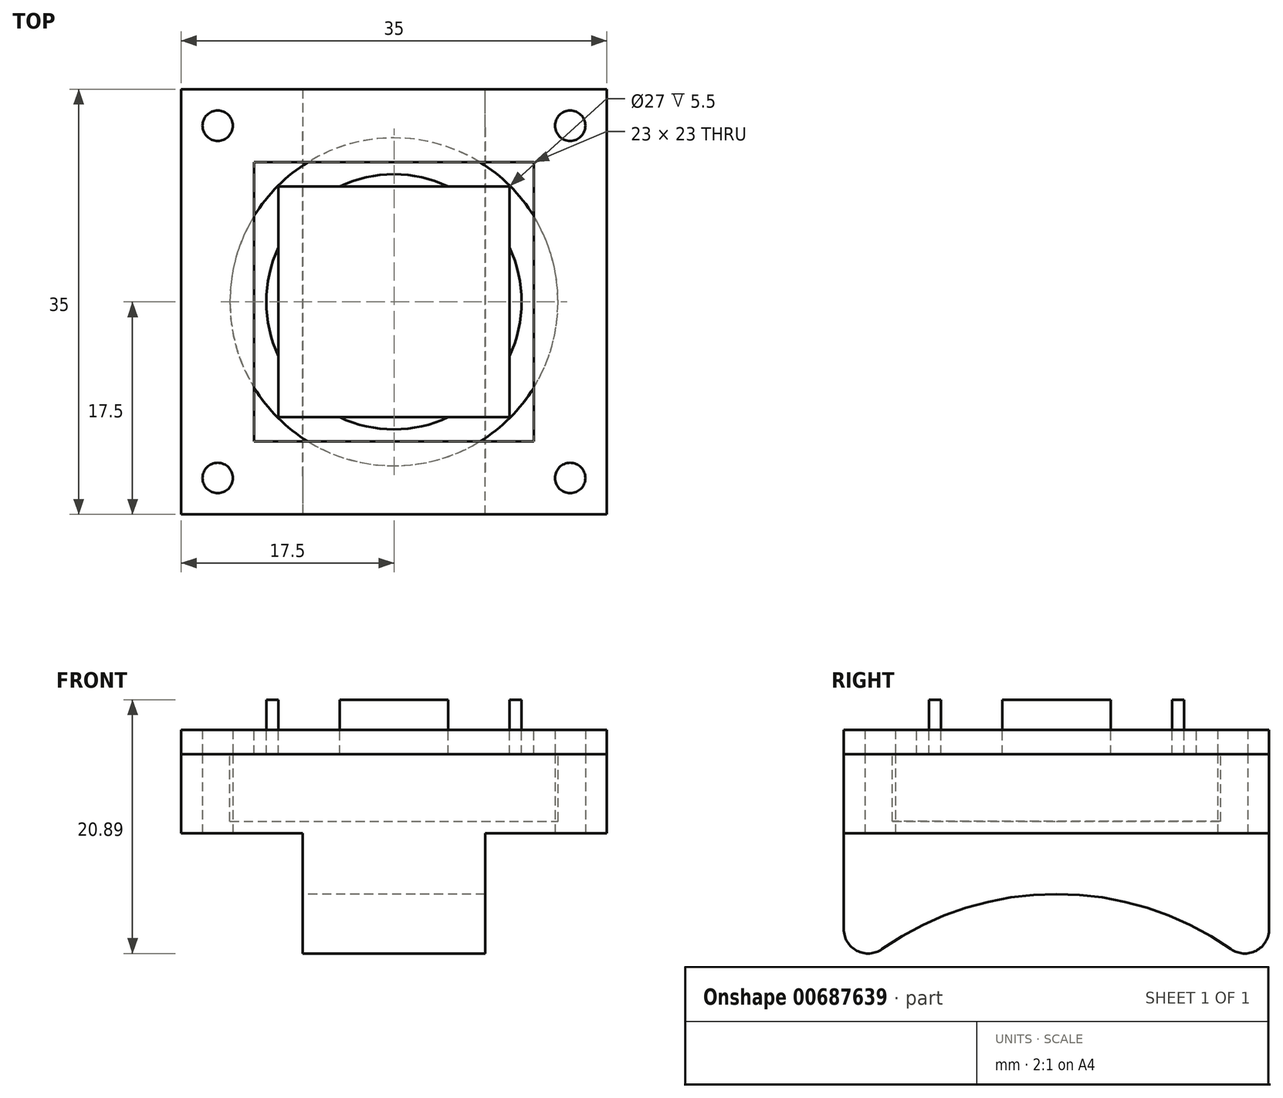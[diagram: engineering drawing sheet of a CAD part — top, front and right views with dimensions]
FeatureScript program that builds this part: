
annotation { "Feature Type Name" : "Feature", "Feature Type Description" : "" }
export const myFeature = defineFeature(function(context is Context, id is Id, definition is map)
    precondition{}
    {
        {
            var Q0;
            Q0=qCreatedBy(makeId("Top.planeOp"),FACE);
            var sketch = newSketch(context, id + "F0", { "sketchPlane" : qUnion([Q0])});
            skLineSegment(sketch, "E0", {"start": v(0, 0) * mm, "end": v(-19, 0) * mm});
            skLineSegment(sketch, "E1", {"start": v(-19, 0) * mm, "end": v(-19, 19) * mm});
            skLineSegment(sketch, "E2", {"start": v(-19, 19) * mm, "end": v(0, 19) * mm});
            skLineSegment(sketch, "E3", {"start": v(0, 19) * mm, "end": v(0, 0) * mm});
            skLineSegment(sketch, "E4.0", {"start": v(2, -2) * mm, "end": v(-21, -2) * mm});
            skLineSegment(sketch, "E4.1", {"start": v(2, 21) * mm, "end": v(2, -2) * mm});
            skLineSegment(sketch, "E4.2", {"start": v(-21, 21) * mm, "end": v(2, 21) * mm});
            skLineSegment(sketch, "E4.3", {"start": v(-21, -2) * mm, "end": v(-21, 21) * mm});
            skCircle(sketch, "E5", {"center": v(-9.5, 9.5) * mm, "radius": 10.5 * mm});
            skPoint(sketch, "E5.centerSnap0", {"position": v(-9.5, 0) * mm});
            skPoint(sketch, "E5.centerSnap1", {"position": v(0, 9.5) * mm});
            skLineSegment(sketch, "E6.0", {"start": v(8, -8) * mm, "end": v(-27, -8) * mm});
            skLineSegment(sketch, "E6.1", {"start": v(8, 27) * mm, "end": v(8, -8) * mm});
            skLineSegment(sketch, "E6.2", {"start": v(-27, 27) * mm, "end": v(8, 27) * mm});
            skLineSegment(sketch, "E6.3", {"start": v(-27, -8) * mm, "end": v(-27, 27) * mm});
            skLineSegment(sketch, "E7", {"start": v(-27, -8) * mm, "end": v(-21, -2) * mm});
            skLineSegment(sketch, "E8", {"start": v(-27, -8) * mm, "end": v(-24, -5) * mm});
            skLineSegment(sketch, "E9", {"start": v(-9.5, 9.5) * mm, "end": v(-11.5, 9.5) * mm});
            skLineSegment(sketch, "E10", {"start": v(-9.5, 9.5) * mm, "end": v(-9.5, 11.53) * mm});
            skLineSegment(sketch, "E11.MirrorCS", {"start": v(-27, 27) * mm, "end": v(-24, 24) * mm});
            skLineSegment(sketch, "E12.MirrorCS", {"start": v(8, -8) * mm, "end": v(5, -5) * mm});
            skLineSegment(sketch, "E13.MirrorCS", {"start": v(8, 27) * mm, "end": v(5, 24) * mm});
            skSolve(sketch);
        }
        {
            var Q0;
            Q0 = qSketchRegion(id + "F0", true);
            var Q1;
            {var subQ0=sQuery(id+"F0.wireOp",EDGE,"E5");var subQ1=sQuery(id+"F0.wireOp",EDGE,"E3");var subQ2=makeQuery(id+"F0.imprint","INTERSECT",VERTEX,{"disambiguationData":[OD(0.0)],"derivedFrom":[subQ1,subQ0]});Q1=makeQuery(id+"F0.imprint","IMPRINT",FACE,{"disambiguationData":[TD([[makeQuery(id+"F0.imprint","IMPRINT",EDGE,{"disambiguationData":[TD([[subQ2,-1.0]])],"derivedFrom":subQ1}),1.0]])]});}
            var Q2;
            {var subQ0=sQuery(id+"F0.wireOp",EDGE,"E5");var subQ1=sQuery(id+"F0.wireOp",EDGE,"E0");var subQ2=makeQuery(id+"F0.imprint","INTERSECT",VERTEX,{"disambiguationData":[OD(0.0)],"derivedFrom":[subQ1,subQ0]});Q2=makeQuery(id+"F0.imprint","IMPRINT",FACE,{"disambiguationData":[TD([[makeQuery(id+"F0.imprint","IMPRINT",EDGE,{"disambiguationData":[TD([[subQ2,-1.0]])],"derivedFrom":subQ1}),1.0]])]});}
            var Q3;
            {var subQ0=sQuery(id+"F0.wireOp",EDGE,"E5");var subQ1=sQuery(id+"F0.wireOp",EDGE,"E1");var subQ2=makeQuery(id+"F0.imprint","INTERSECT",VERTEX,{"disambiguationData":[OD(0.0)],"derivedFrom":[subQ1,subQ0]});Q3=makeQuery(id+"F0.imprint","IMPRINT",FACE,{"disambiguationData":[TD([[makeQuery(id+"F0.imprint","IMPRINT",EDGE,{"disambiguationData":[TD([[subQ2,-1.0]])],"derivedFrom":subQ1}),1.0]])]});}
            var Q4;
            {var subQ0=sQuery(id+"F0.wireOp",EDGE,"E5");var subQ1=sQuery(id+"F0.wireOp",EDGE,"E2");var subQ2=makeQuery(id+"F0.imprint","INTERSECT",VERTEX,{"disambiguationData":[OD(0.0)],"derivedFrom":[subQ1,subQ0]});Q4=makeQuery(id+"F0.imprint","IMPRINT",FACE,{"disambiguationData":[TD([[makeQuery(id+"F0.imprint","IMPRINT",EDGE,{"disambiguationData":[TD([[subQ2,-1.0]])],"derivedFrom":subQ1}),1.0]])]});}
            var Q5;
            {var subQ0=sQuery(id+"F0.wireOp",EDGE,"E2");var subQ1=sQuery(id+"F0.wireOp",EDGE,"E1");var subQ2=makeQuery(id+"F0.imprint","INTERSECT",VERTEX,{"derivedFrom":[subQ1,subQ0]});Q5=makeQuery(id+"F0.imprint","IMPRINT",FACE,{"disambiguationData":[TD([[makeQuery(id+"F0.imprint","IMPRINT",EDGE,{"disambiguationData":[TD([[subQ2,1.0]])],"derivedFrom":subQ1}),-1.0]])]});}
            var Q6;
            {var subQ0=sQuery(id+"F0.wireOp",EDGE,"E3");var subQ1=sQuery(id+"F0.wireOp",EDGE,"E2");var subQ2=makeQuery(id+"F0.imprint","INTERSECT",VERTEX,{"derivedFrom":[subQ1,subQ0]});Q6=makeQuery(id+"F0.imprint","IMPRINT",FACE,{"disambiguationData":[TD([[makeQuery(id+"F0.imprint","IMPRINT",EDGE,{"disambiguationData":[TD([[subQ2,1.0]])],"derivedFrom":subQ1}),-1.0]])]});}
            var Q7;
            {var subQ0=sQuery(id+"F0.wireOp",EDGE,"E3");var subQ1=sQuery(id+"F0.wireOp",EDGE,"E0");var subQ2=makeQuery(id+"F0.imprint","INTERSECT",VERTEX,{"derivedFrom":[subQ1,subQ0]});Q7=makeQuery(id+"F0.imprint","IMPRINT",FACE,{"disambiguationData":[TD([[makeQuery(id+"F0.imprint","IMPRINT",EDGE,{"disambiguationData":[TD([[subQ2,-1.0]])],"derivedFrom":subQ1}),-1.0]])]});}
            var Q8;
            {var subQ0=sQuery(id+"F0.wireOp",EDGE,"E1");var subQ1=sQuery(id+"F0.wireOp",EDGE,"E0");var subQ2=makeQuery(id+"F0.imprint","INTERSECT",VERTEX,{"derivedFrom":[subQ1,subQ0]});Q8=makeQuery(id+"F0.imprint","IMPRINT",FACE,{"disambiguationData":[TD([[makeQuery(id+"F0.imprint","IMPRINT",EDGE,{"disambiguationData":[TD([[subQ2,1.0]])],"derivedFrom":subQ1}),-1.0]])]});}
            var Q9;
            Q9=makeQuery(id+"F0.imprint","IMPRINT",FACE,{"disambiguationData":[TD([[makeQuery(id+"F0.imprint","IMPRINT",EDGE,{"derivedFrom":sQuery(id+"F0.wireOp",EDGE,"E4.0")}),-1.0]])]});
            var Q10;
            {var subQ0=sQuery(id+"F0.wireOp",EDGE,"E5");var subQ10=sQuery(id+"F0.wireOp",EDGE,"E0");var subQ11=makeQuery(id+"F0.imprint","INTERSECT",VERTEX,{"disambiguationData":[OD(0.0)],"derivedFrom":[subQ10,subQ0]});Q10=makeQuery(id+"F0.imprint","IMPRINT",FACE,{"disambiguationData":[TD([[makeQuery(id+"F0.imprint","IMPRINT",EDGE,{"disambiguationData":[TD([[subQ11,-1.0]])],"derivedFrom":subQ10}),-1.0]])]});}
            extrude(context, id + "F1", {"entities" : qUnion([Q0, Q1, Q2, Q3, Q4, Q5, Q6, Q7, Q8, Q9, Q10]), "oppositeDirection" : true, "depth" : 2 * mm, "offsetDistance" : 25 * mm});
        }
        {
            var Q0;
            Q0=makeQuery(id+"F1.opExtrude","CAP_FACE",FACE,{"disambiguationData":[OSD([sQuery(id+"F0.wireOp",EDGE,"E6.0"),sQuery(id+"F0.wireOp",EDGE,"E6.1"),sQuery(id+"F0.wireOp",EDGE,"E6.2"),sQuery(id+"F0.wireOp",EDGE,"E6.3")])],"isStart":false});
            var sketch = newSketch(context, id + "F2", { "sketchPlane" : qUnion([Q0])});
            skLineSegment(sketch, "E14", {"start": v(-27, -27) * mm, "end": v(-27, 8) * mm});
            skLineSegment(sketch, "E15", {"start": v(-27, 8) * mm, "end": v(8, 8) * mm});
            skLineSegment(sketch, "E16", {"start": v(8, 8) * mm, "end": v(8, -27) * mm});
            skLineSegment(sketch, "E17", {"start": v(8, -27) * mm, "end": v(-27, -27) * mm});
            skLineSegment(sketch, "E18", {"start": v(-27, -9.5) * mm, "end": v(8, -9.5) * mm});
            skCircle(sketch, "E19", {"center": v(-9.5, -9.5) * mm, "radius": 13.5 * mm});
            skSolve(sketch);
        }
        {
            var Q0;
            Q0 = qSketchRegion(id + "F2", true);
            extrude(context, id + "F3", {"entities" : qUnion([Q0]), "depth" : 5.5 * mm, "offsetDistance" : 25 * mm});
        }
        {
            var Q0;
            {var subQ0=sQuery(id+"F0.wireOp",EDGE,"E5");var subQ1=sQuery(id+"F0.wireOp",EDGE,"E1");var subQ2=makeQuery(id+"F0.imprint","INTERSECT",VERTEX,{"disambiguationData":[OD(0.0)],"derivedFrom":[subQ1,subQ0]});Q0=makeQuery(id+"F0.imprint","IMPRINT",FACE,{"disambiguationData":[TD([[makeQuery(id+"F0.imprint","IMPRINT",EDGE,{"disambiguationData":[TD([[subQ2,-1.0]])],"derivedFrom":subQ1}),1.0]])]});}
            var Q1;
            {var subQ0=sQuery(id+"F0.wireOp",EDGE,"E5");var subQ1=sQuery(id+"F0.wireOp",EDGE,"E2");var subQ2=makeQuery(id+"F0.imprint","INTERSECT",VERTEX,{"disambiguationData":[OD(0.0)],"derivedFrom":[subQ1,subQ0]});Q1=makeQuery(id+"F0.imprint","IMPRINT",FACE,{"disambiguationData":[TD([[makeQuery(id+"F0.imprint","IMPRINT",EDGE,{"disambiguationData":[TD([[subQ2,-1.0]])],"derivedFrom":subQ1}),1.0]])]});}
            var Q2;
            {var subQ0=sQuery(id+"F0.wireOp",EDGE,"E5");var subQ1=sQuery(id+"F0.wireOp",EDGE,"E3");var subQ2=makeQuery(id+"F0.imprint","INTERSECT",VERTEX,{"disambiguationData":[OD(0.0)],"derivedFrom":[subQ1,subQ0]});Q2=makeQuery(id+"F0.imprint","IMPRINT",FACE,{"disambiguationData":[TD([[makeQuery(id+"F0.imprint","IMPRINT",EDGE,{"disambiguationData":[TD([[subQ2,-1.0]])],"derivedFrom":subQ1}),1.0]])]});}
            var Q3;
            {var subQ0=sQuery(id+"F0.wireOp",EDGE,"E5");var subQ1=sQuery(id+"F0.wireOp",EDGE,"E0");var subQ2=makeQuery(id+"F0.imprint","INTERSECT",VERTEX,{"disambiguationData":[OD(0.0)],"derivedFrom":[subQ1,subQ0]});Q3=makeQuery(id+"F0.imprint","IMPRINT",FACE,{"disambiguationData":[TD([[makeQuery(id+"F0.imprint","IMPRINT",EDGE,{"disambiguationData":[TD([[subQ2,-1.0]])],"derivedFrom":subQ1}),1.0]])]});}
            var Q4;
            Q4=makeQuery(id+"F0.imprint","IMPRINT",FACE,{"disambiguationData":[TD([[makeQuery(id+"F0.imprint","IMPRINT",EDGE,{"derivedFrom":sQuery(id+"F0.wireOp",EDGE,"E4.0")}),-1.0]])]});
            extrude(context, id + "F4", {"entities" : qUnion([Q0, Q1, Q2, Q3, Q4]), "operationType" : NewBodyOperationType.ADD, "depth" : 2.5 * mm, "offsetDistance" : 25 * mm});
        }
        {
            var Q0;
            Q0=makeQuery(id+"F3.opExtrude","CAP_FACE",FACE,{"disambiguationData":[OSD([sQuery(id+"F2.wireOp",EDGE,"E14"),sQuery(id+"F2.wireOp",EDGE,"E15"),sQuery(id+"F2.wireOp",EDGE,"E16"),sQuery(id+"F2.wireOp",EDGE,"E17"),sQuery(id+"F2.wireOp",EDGE,"E19")])],"isStart":false});
            var Q1;
            Q1=makeQuery(id+"F1.opExtrude","CAP_FACE",FACE,{"disambiguationData":[OSD([sQuery(id+"F0.wireOp",EDGE,"E6.0"),sQuery(id+"F0.wireOp",EDGE,"E6.1"),sQuery(id+"F0.wireOp",EDGE,"E6.2"),sQuery(id+"F0.wireOp",EDGE,"E6.3")])],"isStart":false});
            extrude(context, id + "F5", {"entities" : qUnion([Q0, Q1]), "depth" : 1 * mm, "offsetDistance" : 25 * mm});
        }
        {
            var Q0;
            Q0=makeQuery(id+"F5.opExtrude","SWEPT_BODY",BODY,{"disambiguationData":[OSD([sQuery(id+"F2.wireOp",EDGE,"E14"),sQuery(id+"F2.wireOp",EDGE,"E15"),sQuery(id+"F2.wireOp",EDGE,"E16"),sQuery(id+"F2.wireOp",EDGE,"E17"),sQuery(id+"F2.wireOp",EDGE,"E19")])]});
            var Q1;
            Q1=makeQuery(id+"F5.opExtrude","SWEPT_BODY",BODY,{"disambiguationData":[OSD([sQuery(id+"F0.wireOp",EDGE,"E6.0"),sQuery(id+"F0.wireOp",EDGE,"E6.1"),sQuery(id+"F0.wireOp",EDGE,"E6.2"),sQuery(id+"F0.wireOp",EDGE,"E6.3")])]});
            deleteBodies(context, id + "F6", {"entities" : qUnion([Q0, Q1])});
        }
        {
            var Q0;
            Q0=makeQuery(id+"F3.opExtrude","CAP_FACE",FACE,{"disambiguationData":[OSD([sQuery(id+"F2.wireOp",EDGE,"E14"),sQuery(id+"F2.wireOp",EDGE,"E15"),sQuery(id+"F2.wireOp",EDGE,"E16"),sQuery(id+"F2.wireOp",EDGE,"E17"),sQuery(id+"F2.wireOp",EDGE,"E19")])],"isStart":false});
            var sketch = newSketch(context, id + "F7", { "sketchPlane" : qUnion([Q0])});
            skLineSegment(sketch, "E20", {"start": v(-27, -27) * mm, "end": v(8, -27) * mm});
            skLineSegment(sketch, "E21", {"start": v(8, -27) * mm, "end": v(8, 8) * mm});
            skLineSegment(sketch, "E22", {"start": v(8, 8) * mm, "end": v(-27, 8) * mm});
            skLineSegment(sketch, "E23", {"start": v(-27, 8) * mm, "end": v(-27, -27) * mm});
            skSolve(sketch);
        }
        {
            var Q0;
            Q0=makeQuery(id+"F7.imprint","IMPRINT",FACE,{"disambiguationData":[TD([[makeQuery(id+"F7.imprint","IMPRINT",EDGE,{"derivedFrom":sQuery(id+"F7.wireOp",EDGE,"E20")}),1.0]])]});
            var Q1;
            Q1=makeQuery(id+"F7.imprint","IMPRINT",FACE,{"disambiguationData":[TD([[makeQuery(id+"F7.imprint","IMPRINT",EDGE,{"derivedFrom":makeQuery(id+"FP3SZp29wrBzVes_1.hole-0.boolean.opBoolean","INTERSECT",EDGE,{"derivedFrom":[makeQuery(id+"F3.opExtrude","CAP_FACE",FACE,{"disambiguationData":[OSD([sQuery(id+"F2.wireOp",EDGE,"E14"),sQuery(id+"F2.wireOp",EDGE,"E15"),sQuery(id+"F2.wireOp",EDGE,"E16"),sQuery(id+"F2.wireOp",EDGE,"E17"),sQuery(id+"F2.wireOp",EDGE,"E19")])],"isStart":false}),makeQuery(id+"FP3SZp29wrBzVes_1.hole-0.opRevolve","SWEPT_FACE",FACE,{"disambiguationData":[OSD([sQuery(id+"FP3SZp29wrBzVes_1.hole-0.sketch.wireOp",EDGE,"core_line_2")])]})]})}),-1.0]])]});
            var Q2;
            Q2=makeQuery(id+"F7.imprint","IMPRINT",FACE,{"disambiguationData":[TD([[makeQuery(id+"F7.imprint","IMPRINT",EDGE,{"derivedFrom":makeQuery(id+"FP3SZp29wrBzVes_1.hole-1.boolean.opBoolean","INTERSECT",EDGE,{"derivedFrom":[makeQuery(id+"F3.opExtrude","CAP_FACE",FACE,{"disambiguationData":[OSD([sQuery(id+"F2.wireOp",EDGE,"E14"),sQuery(id+"F2.wireOp",EDGE,"E15"),sQuery(id+"F2.wireOp",EDGE,"E16"),sQuery(id+"F2.wireOp",EDGE,"E17"),sQuery(id+"F2.wireOp",EDGE,"E19")])],"isStart":false}),makeQuery(id+"FP3SZp29wrBzVes_1.hole-1.opRevolve","SWEPT_FACE",FACE,{"disambiguationData":[OSD([sQuery(id+"FP3SZp29wrBzVes_1.hole-1.sketch.wireOp",EDGE,"core_line_2")])]})]})}),-1.0]])]});
            var Q3;
            Q3=makeQuery(id+"F7.imprint","IMPRINT",FACE,{"disambiguationData":[TD([[makeQuery(id+"F7.imprint","IMPRINT",EDGE,{"derivedFrom":makeQuery(id+"FP3SZp29wrBzVes_1.hole-3.boolean.opBoolean","INTERSECT",EDGE,{"derivedFrom":[makeQuery(id+"F3.opExtrude","CAP_FACE",FACE,{"disambiguationData":[OSD([sQuery(id+"F2.wireOp",EDGE,"E14"),sQuery(id+"F2.wireOp",EDGE,"E15"),sQuery(id+"F2.wireOp",EDGE,"E16"),sQuery(id+"F2.wireOp",EDGE,"E17"),sQuery(id+"F2.wireOp",EDGE,"E19")])],"isStart":false}),makeQuery(id+"FP3SZp29wrBzVes_1.hole-3.opRevolve","SWEPT_FACE",FACE,{"disambiguationData":[OSD([sQuery(id+"FP3SZp29wrBzVes_1.hole-3.sketch.wireOp",EDGE,"core_line_2")])]})]})}),-1.0]])]});
            var Q4;
            Q4=makeQuery(id+"F7.imprint","IMPRINT",FACE,{"disambiguationData":[TD([[makeQuery(id+"F7.imprint","IMPRINT",EDGE,{"derivedFrom":makeQuery(id+"F3.opExtrude","CAP_EDGE",EDGE,{"disambiguationData":[OSD([sQuery(id+"F2.wireOp",EDGE,"E19")])],"isStart":false})}),1.0]])]});
            var Q5;
            Q5=makeQuery(id+"F7.imprint","IMPRINT",FACE,{"disambiguationData":[TD([[makeQuery(id+"F7.imprint","IMPRINT",EDGE,{"derivedFrom":makeQuery(id+"FP3SZp29wrBzVes_1.hole-2.boolean.opBoolean","INTERSECT",EDGE,{"derivedFrom":[makeQuery(id+"F3.opExtrude","CAP_FACE",FACE,{"disambiguationData":[OSD([sQuery(id+"F2.wireOp",EDGE,"E14"),sQuery(id+"F2.wireOp",EDGE,"E15"),sQuery(id+"F2.wireOp",EDGE,"E16"),sQuery(id+"F2.wireOp",EDGE,"E17"),sQuery(id+"F2.wireOp",EDGE,"E19")])],"isStart":false}),makeQuery(id+"FP3SZp29wrBzVes_1.hole-2.opRevolve","SWEPT_FACE",FACE,{"disambiguationData":[OSD([sQuery(id+"FP3SZp29wrBzVes_1.hole-2.sketch.wireOp",EDGE,"core_line_2")])]})]})}),-1.0]])]});
            extrude(context, id + "F8", {"entities" : qUnion([Q0, Q1, Q2, Q3, Q4, Q5]), "operationType" : NewBodyOperationType.ADD, "depth" : 1 * mm, "offsetDistance" : 25 * mm});
        }
        {
            var Q0;
            Q0=sQuery(id+"F0.wireOp",VERTEX,"E8.end");
            var Q1;
            Q1=sQuery(id+"F0.wireOp",VERTEX,"E11.MirrorCS.end");
            var Q2;
            Q2=sQuery(id+"F0.wireOp",VERTEX,"E13.MirrorCS.end");
            var Q3;
            Q3=sQuery(id+"F0.wireOp",VERTEX,"E12.MirrorCS.end");
            var Q4;
            Q4=makeQuery(id+"F3.opExtrude","SWEPT_BODY",BODY,{"disambiguationData":[OSD([sQuery(id+"F2.wireOp",EDGE,"E14"),sQuery(id+"F2.wireOp",EDGE,"E15"),sQuery(id+"F2.wireOp",EDGE,"E16"),sQuery(id+"F2.wireOp",EDGE,"E17"),sQuery(id+"F2.wireOp",EDGE,"E19")])]});
            var Q5;
            Q5=makeQuery(id+"F1.opExtrude","SWEPT_BODY",BODY,{"disambiguationData":[OSD([sQuery(id+"F0.wireOp",EDGE,"E6.0"),sQuery(id+"F0.wireOp",EDGE,"E6.1"),sQuery(id+"F0.wireOp",EDGE,"E6.2"),sQuery(id+"F0.wireOp",EDGE,"E6.3")])]});
            hole(context, id + "F9", {"style" : HoleStyle.SIMPLE, "endStyle" : HoleEndStyle.BLIND, "holeDiameter" : 2.5 * mm, "majorDiameter" : 5 * mm, "holeDepth" : 10 * mm, "isTappedThrough" : true, "tappedDepth" : 12 * mm, "tapClearance" : 3, "locations" : qUnion([Q0, Q1, Q2, Q3]), "scope" : qUnion([Q4, Q5]), "startStyle" : HoleStartStyle.PART});
        }
        {
            var Q0;
            Q0=makeQuery(id+"F8.opExtrude","CAP_FACE",FACE,{"disambiguationData":[OSD([sQuery(id+"F7.wireOp",EDGE,"E20"),sQuery(id+"F7.wireOp",EDGE,"E21"),sQuery(id+"F7.wireOp",EDGE,"E22"),sQuery(id+"F7.wireOp",EDGE,"E23")])],"isStart":false});
            var sketch = newSketch(context, id + "F10", { "sketchPlane" : qUnion([Q0])});
            skLineSegment(sketch, "E24", {"start": v(-27, 8) * mm, "end": v(8, 8) * mm});
            skLineSegment(sketch, "E25", {"start": v(8, 8) * mm, "end": v(8, -27) * mm});
            skLineSegment(sketch, "E26", {"start": v(8, -27) * mm, "end": v(-27, -27) * mm});
            skLineSegment(sketch, "E27", {"start": v(-27, -27) * mm, "end": v(-27, 8) * mm});
            skLineSegment(sketch, "E28", {"start": v(-9.5, 8) * mm, "end": v(-9.5, -27) * mm});
            skLineSegment(sketch, "E29", {"start": v(-9.5, -9.5) * mm, "end": v(-17, -9.5) * mm});
            skLineSegment(sketch, "E30", {"start": v(-17, -9.5) * mm, "end": v(-17, 8) * mm});
            skLineSegment(sketch, "E31.MirrorCS", {"start": v(-2, -9.5) * mm, "end": v(-2, 8) * mm});
            skLineSegment(sketch, "E32.MirrorCS", {"start": v(-17, -9.5) * mm, "end": v(-17, -27) * mm});
            skLineSegment(sketch, "E33.MirrorCS", {"start": v(-2, -9.5) * mm, "end": v(-2, -27) * mm});
            skSolve(sketch);
        }
        {
            var Q0;
            {var subQ4=sQuery(id+"F10.wireOp",EDGE,"E29");Q0=makeQuery(id+"F10.imprint","IMPRINT",FACE,{"disambiguationData":[TD([[makeQuery(id+"F10.imprint","IMPRINT",EDGE,{"derivedFrom":subQ4}),-1.0]])]});}
            var Q1;
            {var subQ4=sQuery(id+"F10.wireOp",EDGE,"E29");Q1=makeQuery(id+"F10.imprint","IMPRINT",FACE,{"disambiguationData":[TD([[makeQuery(id+"F10.imprint","IMPRINT",EDGE,{"derivedFrom":subQ4}),1.0]])]});}
            var Q2;
            {var subQ7=sQuery(id+"F10.wireOp",EDGE,"E31.MirrorCS");Q2=makeQuery(id+"F10.imprint","IMPRINT",FACE,{"disambiguationData":[TD([[makeQuery(id+"F10.imprint","IMPRINT",EDGE,{"derivedFrom":subQ7}),1.0]])]});}
            extrude(context, id + "F11", {"entities" : qUnion([Q0, Q1, Q2]), "operationType" : NewBodyOperationType.ADD, "depth" : 25 * mm, "offsetDistance" : 25 * mm});
        }
        {
            var Q0;
            Q0=makeQuery(id+"F11.opExtrude","SWEPT_FACE",FACE,{"disambiguationData":[OSD([sQuery(id+"F10.wireOp",EDGE,"E30"),sQuery(id+"F10.wireOp",EDGE,"E32.MirrorCS")])]});
            var sketch = newSketch(context, id + "F12", { "sketchPlane" : qUnion([Q0])});
            skLineSegment(sketch, "E34", {"start": v(-9.5, -33.5) * mm, "end": v(-9.5, -38.5) * mm});
            skCircle(sketch, "E35", {"center": v(-9.5, -38.5) * mm, "radius": 25 * mm});
            skSolve(sketch);
        }
        {
            var Q0;
            Q0 = qSketchRegion(id + "F12", true);
            extrude(context, id + "F13", {"entities" : qUnion([Q0]), "operationType" : NewBodyOperationType.REMOVE, "oppositeDirection" : true, "depth" : 25 * mm, "offsetDistance" : 25 * mm});
        }
        {
            var Q0;
            Q0=makeQuery(id+"F13.boolean.opBoolean","INTERSECT",EDGE,{"derivedFrom":[makeQuery(id+"F11.boolean.opBoolean","MERGE",FACE,{"derivedFrom":[makeQuery(id+"F8.boolean.opBoolean","MERGE",FACE,{"derivedFrom":[makeQuery(id+"F3.opExtrude","SWEPT_FACE",FACE,{"disambiguationData":[OSD([sQuery(id+"F2.wireOp",EDGE,"E15")])]}),makeQuery(id+"F8.opExtrude","SWEPT_FACE",FACE,{"disambiguationData":[OSD([sQuery(id+"F7.wireOp",EDGE,"E22")])]})]}),makeQuery(id+"F11.opExtrude","SWEPT_FACE",FACE,{"disambiguationData":[OSD([sQuery(id+"F10.wireOp",EDGE,"E24")])]})]}),makeQuery(id+"F13.opExtrude","SWEPT_FACE",FACE,{"disambiguationData":[OSD([sQuery(id+"F12.wireOp",EDGE,"E35")])]})]});
            var Q1;
            Q1=makeQuery(id+"F13.boolean.opBoolean","INTERSECT",EDGE,{"derivedFrom":[makeQuery(id+"F11.boolean.opBoolean","MERGE",FACE,{"derivedFrom":[makeQuery(id+"F8.boolean.opBoolean","MERGE",FACE,{"derivedFrom":[makeQuery(id+"F3.opExtrude","SWEPT_FACE",FACE,{"disambiguationData":[OSD([sQuery(id+"F2.wireOp",EDGE,"E17")])]}),makeQuery(id+"F8.opExtrude","SWEPT_FACE",FACE,{"disambiguationData":[OSD([sQuery(id+"F7.wireOp",EDGE,"E20")])]})]}),makeQuery(id+"F11.opExtrude","SWEPT_FACE",FACE,{"disambiguationData":[OSD([sQuery(id+"F10.wireOp",EDGE,"E26")])]})]}),makeQuery(id+"F13.opExtrude","SWEPT_FACE",FACE,{"disambiguationData":[OSD([sQuery(id+"F12.wireOp",EDGE,"E35")])]})]});
            fillet(context, id + "F14", {"entities" : qUnion([Q0, Q1]), "radius" : 2 * mm, "tangentPropagation" : true, "allowEdgeOverflow" : false});
        }
    });
